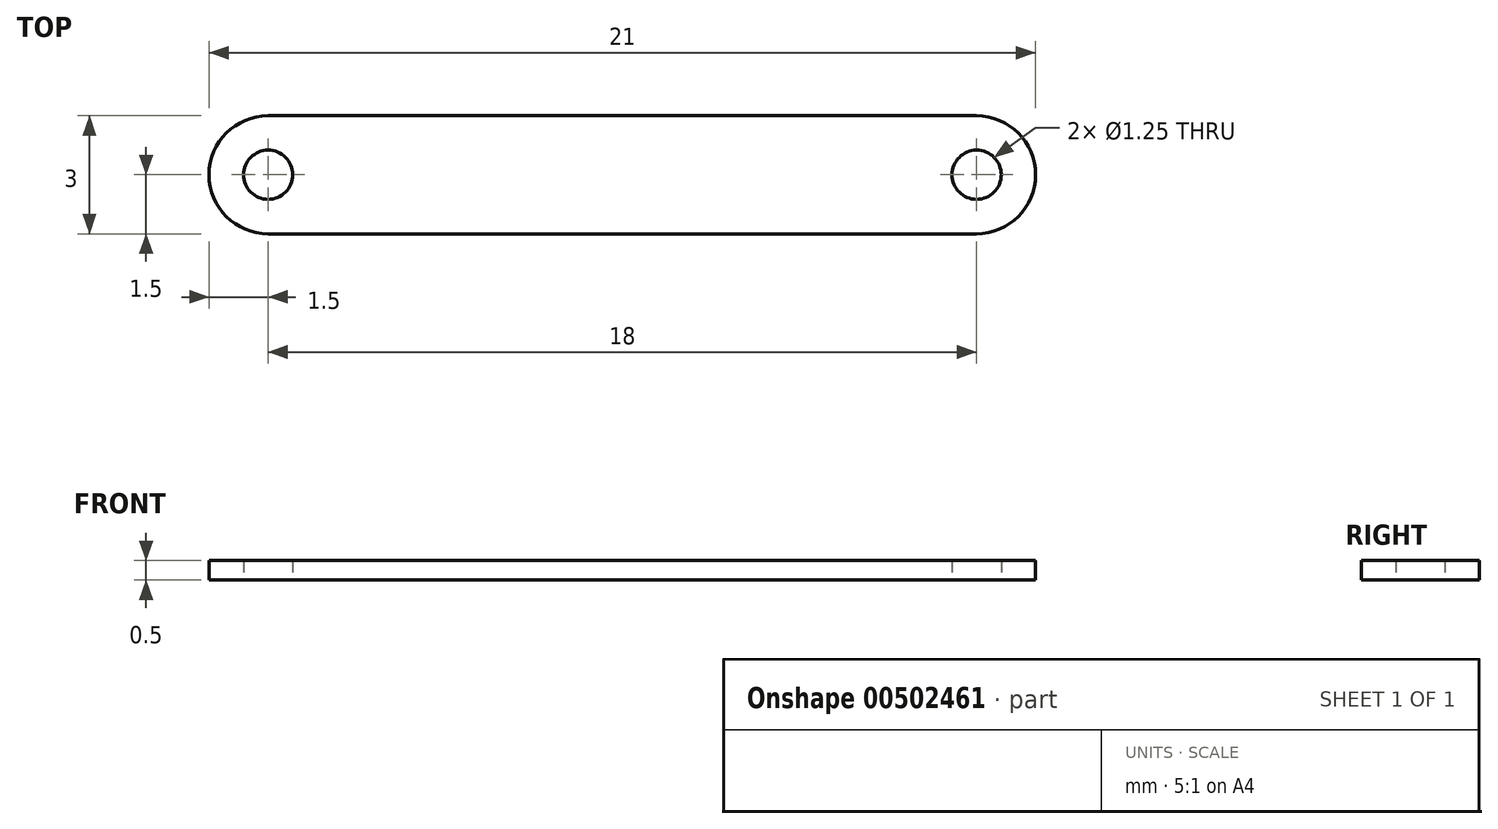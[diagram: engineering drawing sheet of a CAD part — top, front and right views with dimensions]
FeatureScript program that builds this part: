
annotation { "Feature Type Name" : "Feature", "Feature Type Description" : "" }
export const myFeature = defineFeature(function(context is Context, id is Id, definition is map)
    precondition{}
    {
        {
            var Q0;
            Q0=qCreatedBy(makeId("Top.planeOp"),FACE);
            var sketch = newSketch(context, id + "F0", { "sketchPlane" : qUnion([Q0])});
            skLineSegment(sketch, "E0", {"start": v(0, 55.33) * mm, "end": v(0, -43.24) * mm, "construction": true});
            skLineSegment(sketch, "E1", {"start": v(-35.88, 0) * mm, "end": v(33.77, 0) * mm, "construction": true});
            skLineSegment(sketch, "E2.bottom", {"start": v(-10.5, 1.5) * mm, "end": v(10.5, 1.5) * mm});
            skLineSegment(sketch, "E2.top", {"start": v(-10.5, -1.5) * mm, "end": v(10.5, -1.5) * mm});
            skLineSegment(sketch, "E2.left", {"start": v(-10.5, 1.5) * mm, "end": v(-10.5, -1.5) * mm});
            skLineSegment(sketch, "E2.right", {"start": v(10.5, 1.5) * mm, "end": v(10.5, -1.5) * mm});
            skCircle(sketch, "E3", {"center": v(-9, 0) * mm, "radius": 0.62 * mm});
            skCircle(sketch, "E4", {"center": v(9, 0) * mm, "radius": 0.62 * mm});
            skSolve(sketch);
        }
        {
            var Q0;
            Q0=makeQuery(id+"F0.imprint","IMPRINT",FACE,{"disambiguationData":[TD([[makeQuery(id+"F0.imprint","IMPRINT",EDGE,{"derivedFrom":sQuery(id+"F0.wireOp",EDGE,"E2.bottom")}),-1.0]])]});
            extrude(context, id + "F1", {"entities" : qUnion([Q0]), "depth" : 0.5 * mm, "offsetDistance" : 25 * mm});
        }
        {
            var Q0;
            Q0=makeQuery(id+"F1.opExtrude","SWEPT_EDGE",EDGE,{"disambiguationData":[OSD([sQuery(id+"F0.wireOp",EDGE,"E2.top"),sQuery(id+"F0.wireOp",EDGE,"E2.left")])]});
            var Q1;
            Q1=makeQuery(id+"F1.opExtrude","SWEPT_EDGE",EDGE,{"disambiguationData":[OSD([sQuery(id+"F0.wireOp",EDGE,"E2.bottom"),sQuery(id+"F0.wireOp",EDGE,"E2.left")])]});
            var Q2;
            Q2=makeQuery(id+"F1.opExtrude","SWEPT_EDGE",EDGE,{"disambiguationData":[OSD([sQuery(id+"F0.wireOp",EDGE,"E2.top"),sQuery(id+"F0.wireOp",EDGE,"E2.right")])]});
            var Q3;
            Q3=makeQuery(id+"F1.opExtrude","SWEPT_EDGE",EDGE,{"disambiguationData":[OSD([sQuery(id+"F0.wireOp",EDGE,"E2.bottom"),sQuery(id+"F0.wireOp",EDGE,"E2.right")])]});
            fillet(context, id + "F2", {"entities" : qUnion([Q0, Q1, Q2, Q3]), "tangentPropagation" : true, "radius" : 1.5 * mm, "defaultsChanged" : true, "vertexSettings" : [], "allowEdgeOverflow" : false});
        }
    });
